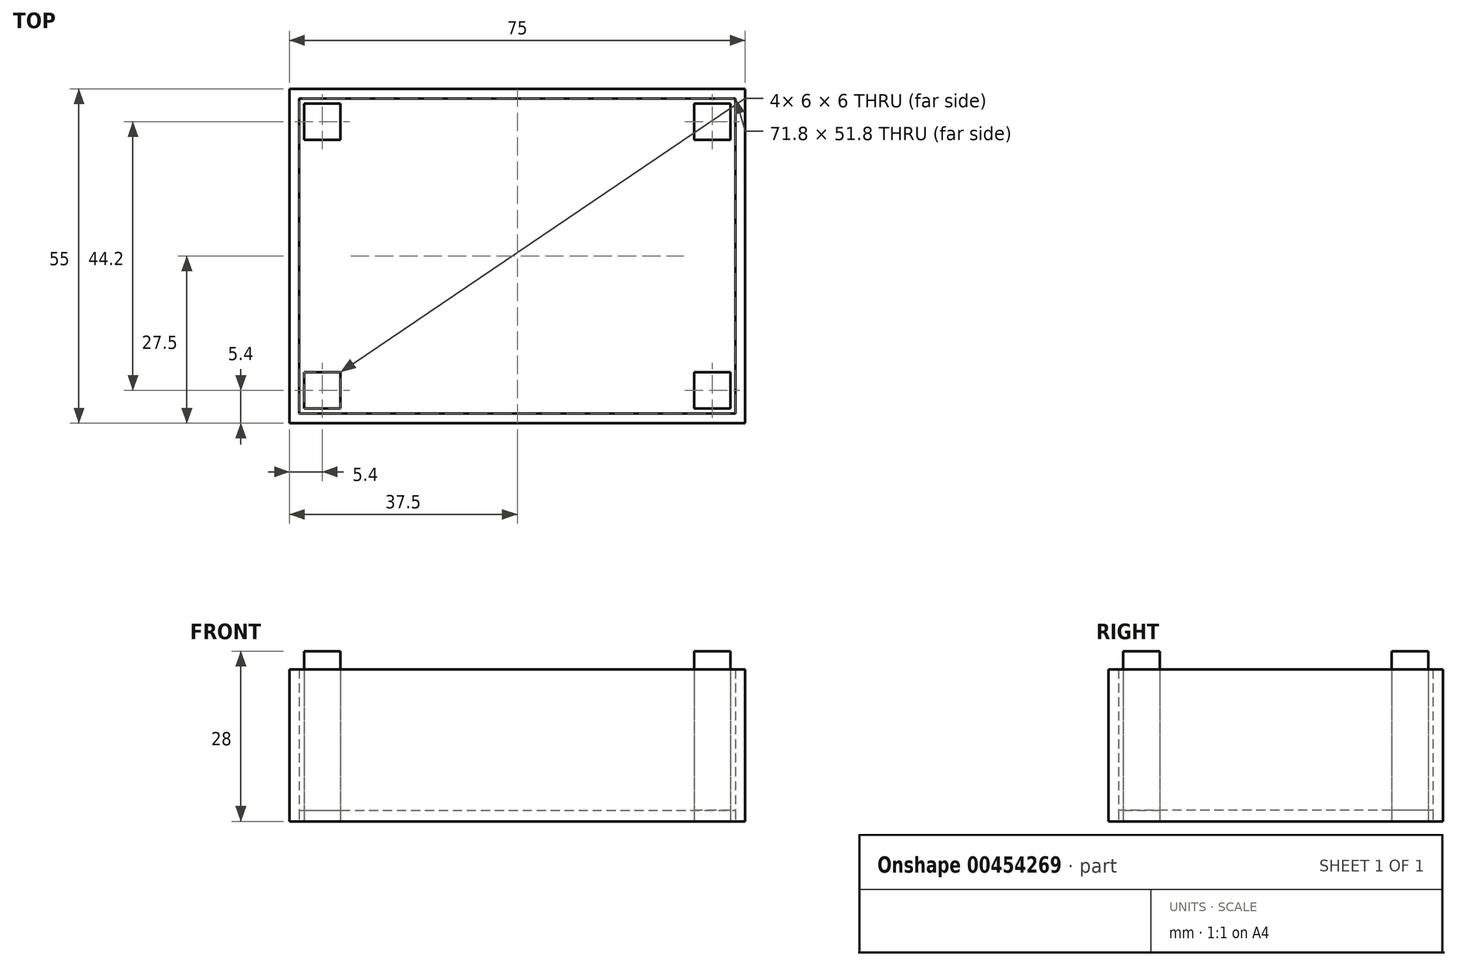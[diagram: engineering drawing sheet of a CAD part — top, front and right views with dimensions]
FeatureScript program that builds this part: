
annotation { "Feature Type Name" : "Feature", "Feature Type Description" : "" }
export const myFeature = defineFeature(function(context is Context, id is Id, definition is map)
    precondition{}
    {
        {
            var Q0;
            Q0=qCreatedBy(makeId("Top.planeOp"),FACE);
            var sketch = newSketch(context, id + "F0", { "sketchPlane" : qUnion([Q0])});
            skLineSegment(sketch, "E0.bottom", {"start": v(-37.5, 27.5) * mm, "end": v(37.5, 27.5) * mm});
            skLineSegment(sketch, "E0.top", {"start": v(-37.5, -27.5) * mm, "end": v(37.5, -27.5) * mm});
            skLineSegment(sketch, "E0.left", {"start": v(-37.5, 27.5) * mm, "end": v(-37.5, -27.5) * mm});
            skLineSegment(sketch, "E0.right", {"start": v(37.5, 27.5) * mm, "end": v(37.5, -27.5) * mm});
            skPoint(sketch, "E0.middle", {"position": v(0, 0) * mm});
            skLineSegment(sketch, "E1.bottom", {"start": v(-35.9, 25.9) * mm, "end": v(35.9, 25.9) * mm});
            skLineSegment(sketch, "E1.top", {"start": v(-35.9, -25.9) * mm, "end": v(35.9, -25.9) * mm});
            skLineSegment(sketch, "E1.left", {"start": v(-35.9, 25.9) * mm, "end": v(-35.9, -25.9) * mm});
            skLineSegment(sketch, "E1.right", {"start": v(35.9, 25.9) * mm, "end": v(35.9, -25.9) * mm});
            skLineSegment(sketch, "E2.bottom", {"start": v(-35.9, 25.9) * mm, "end": v(-35.1, 25.9) * mm});
            skLineSegment(sketch, "E2.left", {"start": v(-35.9, 25.9) * mm, "end": v(-35.9, 25.1) * mm});
            skLineSegment(sketch, "E3.bottom", {"start": v(35.9, 25.9) * mm, "end": v(35.1, 25.9) * mm});
            skLineSegment(sketch, "E3.left", {"start": v(35.9, 25.9) * mm, "end": v(35.9, 25.1) * mm});
            skLineSegment(sketch, "E4.bottom", {"start": v(35.9, -25.9) * mm, "end": v(35.1, -25.9) * mm});
            skLineSegment(sketch, "E4.left", {"start": v(35.9, -25.9) * mm, "end": v(35.9, -25.1) * mm});
            skLineSegment(sketch, "E5.bottom", {"start": v(-35.9, -25.9) * mm, "end": v(-35.1, -25.9) * mm});
            skLineSegment(sketch, "E5.left", {"start": v(-35.9, -25.9) * mm, "end": v(-35.9, -25.1) * mm});
            skLineSegment(sketch, "E6.bottom", {"start": v(-35.1, 25.1) * mm, "end": v(-29.1, 25.1) * mm});
            skLineSegment(sketch, "E6.top", {"start": v(-35.1, 19.1) * mm, "end": v(-29.1, 19.1) * mm});
            skLineSegment(sketch, "E6.left", {"start": v(-35.1, 25.1) * mm, "end": v(-35.1, 19.1) * mm});
            skLineSegment(sketch, "E6.right", {"start": v(-29.1, 25.1) * mm, "end": v(-29.1, 19.1) * mm});
            skLineSegment(sketch, "E7.bottom", {"start": v(35.1, 25.1) * mm, "end": v(29.1, 25.1) * mm});
            skLineSegment(sketch, "E7.top", {"start": v(35.1, 19.1) * mm, "end": v(29.1, 19.1) * mm});
            skLineSegment(sketch, "E7.left", {"start": v(35.1, 25.1) * mm, "end": v(35.1, 19.1) * mm});
            skLineSegment(sketch, "E7.right", {"start": v(29.1, 25.1) * mm, "end": v(29.1, 19.1) * mm});
            skLineSegment(sketch, "E8.bottom", {"start": v(-35.1, -25.1) * mm, "end": v(-29.1, -25.1) * mm});
            skLineSegment(sketch, "E8.top", {"start": v(-35.1, -19.1) * mm, "end": v(-29.1, -19.1) * mm});
            skLineSegment(sketch, "E8.left", {"start": v(-35.1, -25.1) * mm, "end": v(-35.1, -19.1) * mm});
            skLineSegment(sketch, "E8.right", {"start": v(-29.1, -25.1) * mm, "end": v(-29.1, -19.1) * mm});
            skLineSegment(sketch, "E9.bottom", {"start": v(35.1, -25.1) * mm, "end": v(29.1, -25.1) * mm});
            skLineSegment(sketch, "E9.top", {"start": v(35.1, -19.1) * mm, "end": v(29.1, -19.1) * mm});
            skLineSegment(sketch, "E9.left", {"start": v(35.1, -25.1) * mm, "end": v(35.1, -19.1) * mm});
            skLineSegment(sketch, "E9.right", {"start": v(29.1, -25.1) * mm, "end": v(29.1, -19.1) * mm});
            skSolve(sketch);
        }
        {
            var Q0;
            Q0=makeQuery(id+"F0.imprint","IMPRINT",FACE,{"disambiguationData":[TD([[makeQuery(id+"F0.imprint","IMPRINT",EDGE,{"derivedFrom":sQuery(id+"F0.wireOp",EDGE,"E6.bottom")}),-1.0]])]});
            var Q1;
            Q1=makeQuery(id+"F0.imprint","IMPRINT",FACE,{"disambiguationData":[TD([[makeQuery(id+"F0.imprint","IMPRINT",EDGE,{"derivedFrom":sQuery(id+"F0.wireOp",EDGE,"E7.bottom")}),1.0]])]});
            var Q2;
            Q2=makeQuery(id+"F0.imprint","IMPRINT",FACE,{"disambiguationData":[TD([[makeQuery(id+"F0.imprint","IMPRINT",EDGE,{"derivedFrom":sQuery(id+"F0.wireOp",EDGE,"E8.bottom")}),1.0]])]});
            var Q3;
            Q3=makeQuery(id+"F0.imprint","IMPRINT",FACE,{"disambiguationData":[TD([[makeQuery(id+"F0.imprint","IMPRINT",EDGE,{"derivedFrom":sQuery(id+"F0.wireOp",EDGE,"E9.bottom")}),-1.0]])]});
            extrude(context, id + "F1", {"entities" : qUnion([Q0, Q1, Q2, Q3]), "depth" : 28 * mm});
        }
        {
            var Q0;
            Q0=makeQuery(id+"F0.imprint","IMPRINT",FACE,{"disambiguationData":[TD([[makeQuery(id+"F0.imprint","IMPRINT",EDGE,{"derivedFrom":sQuery(id+"F0.wireOp",EDGE,"E0.bottom")}),-1.0]])]});
            extrude(context, id + "F2", {"entities" : qUnion([Q0]), "depth" : 25 * mm});
        }
        {
            var Q0;
            Q0=makeQuery(id+"F0.imprint","IMPRINT",FACE,{"disambiguationData":[TD([[makeQuery(id+"F0.imprint","IMPRINT",EDGE,{"derivedFrom":sQuery(id+"F0.wireOp",EDGE,"E1.bottom")}),-1.0]])]});
            extrude(context, id + "F3", {"entities" : qUnion([Q0]), "depth" : 1.8 * mm});
        }
    });
